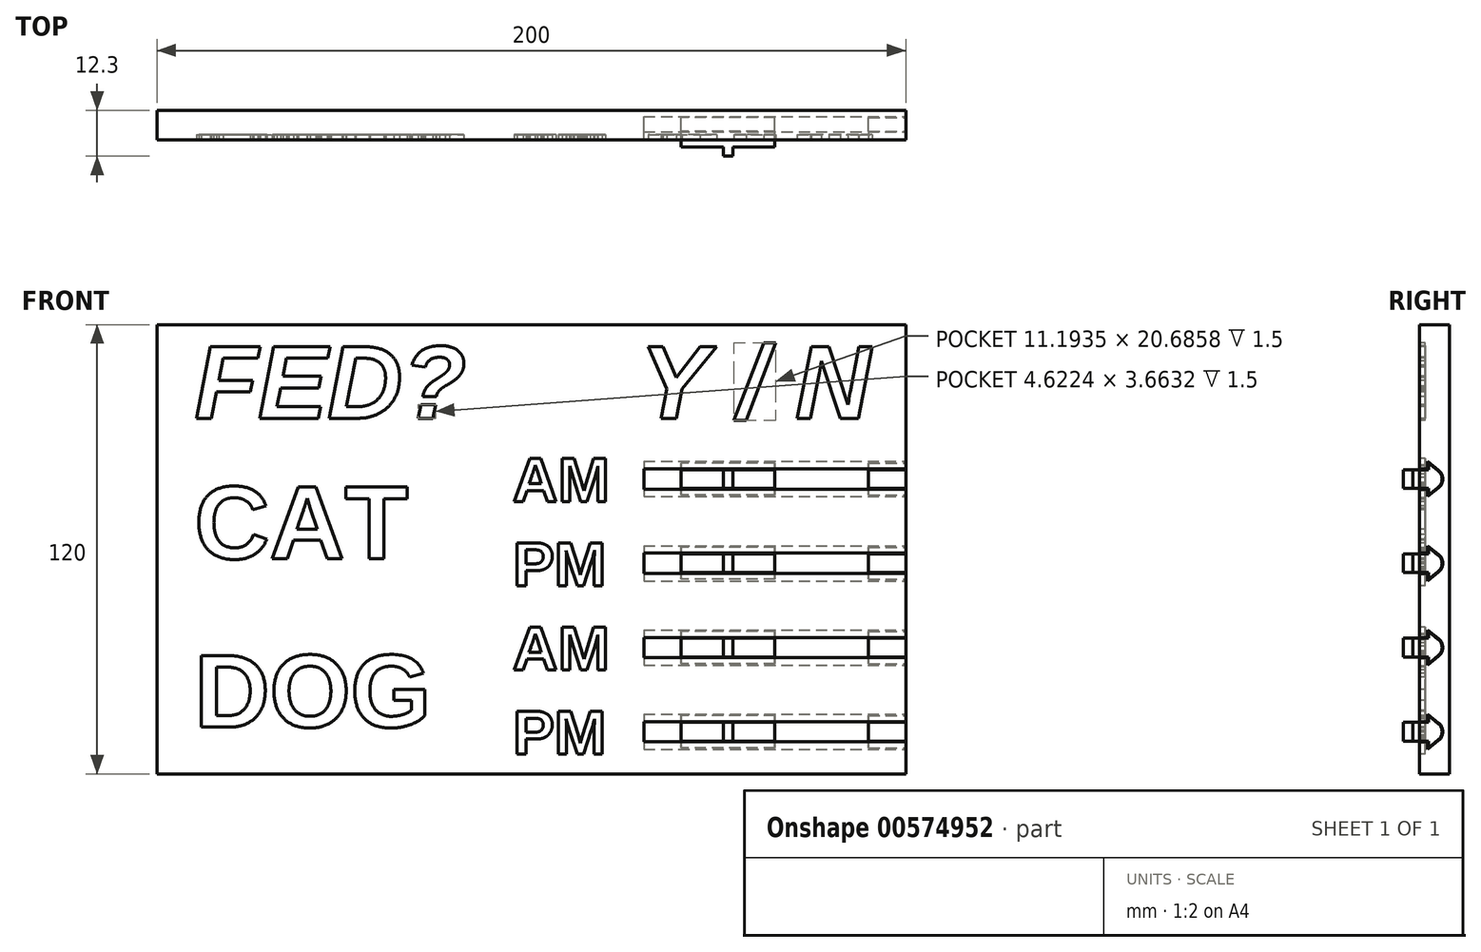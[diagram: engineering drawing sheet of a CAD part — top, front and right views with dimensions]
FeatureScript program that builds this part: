
annotation { "Feature Type Name" : "Feature", "Feature Type Description" : "" }
export const myFeature = defineFeature(function(context is Context, id is Id, definition is map)
    precondition{}
    {
        {
            var Q0;
            Q0=qCreatedBy(makeId("Front.planeOp"),FACE);
            var sketch = newSketch(context, id + "F0", { "sketchPlane" : qUnion([Q0])});
            skLineSegment(sketch, "E0.bottom", {"start": v(100, -60) * mm, "end": v(-100, -60) * mm});
            skLineSegment(sketch, "E0.top", {"start": v(100, 60) * mm, "end": v(-100, 60) * mm});
            skLineSegment(sketch, "E0.left", {"start": v(100, -60) * mm, "end": v(100, 60) * mm});
            skLineSegment(sketch, "E0.right", {"start": v(-100, -60) * mm, "end": v(-100, 60) * mm});
            skPoint(sketch, "E0.middle", {"position": v(0, 0) * mm});
            skSolve(sketch);
        }
        {
            var Q0;
            Q0=qSketchRegion(id+"F0",true);
            extrude(context, id + "F1", {"entities" : qUnion([Q0]), "depth" : 8 * mm, "offsetDistance" : 25 * mm});
        }
        {
            var Q0;
            Q0=makeQuery(id+"F1.opExtrude","CAP_FACE",FACE,{"disambiguationData":[OSD([sQuery(id+"F0.wireOp",EDGE,"E0.bottom"),sQuery(id+"F0.wireOp",EDGE,"E0.top"),sQuery(id+"F0.wireOp",EDGE,"E0.left"),sQuery(id+"F0.wireOp",EDGE,"E0.right")])],"isStart":false});
            var sketch = newSketch(context, id + "F2", { "sketchPlane" : qUnion([Q0])});
            skLineSegment(sketch, "E1", {"start": v(-100, 30) * mm, "end": v(100, 30) * mm, "construction": true});
            skLineSegment(sketch, "E2", {"start": v(-100, 7.5) * mm, "end": v(100, 7.5) * mm, "construction": true});
            skLineSegment(sketch, "E3", {"start": v(-100, -15) * mm, "end": v(100, -15) * mm, "construction": true});
            skLineSegment(sketch, "E4", {"start": v(-100, -37.5) * mm, "end": v(100, -37.5) * mm, "construction": true});
            skLineSegment(sketch, "E5", {"start": v(-100, 7.5) * mm, "end": v(-100, 30) * mm, "construction": true});
            skLineSegment(sketch, "E6", {"start": v(-100, 7.5) * mm, "end": v(-100, -15) * mm, "construction": true});
            skLineSegment(sketch, "E7", {"start": v(-100, -37.5) * mm, "end": v(-100, -15) * mm, "construction": true});
            skLineSegment(sketch, "E8", {"start": v(-100, -60) * mm, "end": v(-100, -37.5) * mm, "construction": true});
            skText(sketch, "E9", { "text": "CAT", "fontName": "Arimo-Bold.ttf"});
            skPoint(sketch, "E10", {"position": v(-90, 7.5) * mm});
            skText(sketch, "E11", { "text": "DOG", "fontName": "Arimo-Bold.ttf"});
            skPoint(sketch, "E12", {"position": v(-90, -37.5) * mm});
            skLineSegment(sketch, "E13", {"start": v(-100, 12.99) * mm, "end": v(-90, 12.99) * mm, "construction": true});
            skLineSegment(sketch, "E14", {"start": v(-100, -31.58) * mm, "end": v(-90, -31.58) * mm, "construction": true});
            skText(sketch, "E15", { "text": "FED?      Y / N", "fontName": "Arimo-BoldItalic.ttf"});
            skPoint(sketch, "E16", {"position": v(-100, 60) * mm});
            skPoint(sketch, "E17", {"position": v(-100, 45) * mm});
            skPoint(sketch, "E18", {"position": v(-90, 45) * mm});
            skLineSegment(sketch, "E19", {"start": v(-90, 50.64) * mm, "end": v(-100, 50.64) * mm, "construction": true});
            skText(sketch, "E20", { "text": "AM", "fontName": "Arimo-Bold.ttf"});
            skPoint(sketch, "E21", {"position": v(-5, 18.75) * mm});
            skText(sketch, "E22", { "text": "PM", "fontName": "Arimo-Bold.ttf"});
            skPoint(sketch, "E23", {"position": v(-5, -3.75) * mm});
            skPoint(sketch, "E24", {"position": v(20.04, -3.75) * mm});
            skPoint(sketch, "E25", {"position": v(20.96, 18.75) * mm});
            skPoint(sketch, "E26", {"position": v(100, 18.75) * mm});
            skPoint(sketch, "E27", {"position": v(100, -3.75) * mm});
            skText(sketch, "E28", { "text": "AM", "fontName": "Arimo-Bold.ttf"});
            skText(sketch, "E29", { "text": "PM", "fontName": "Arimo-Bold.ttf"});
            skPoint(sketch, "E30", {"position": v(100, -26.25) * mm});
            skPoint(sketch, "E31", {"position": v(100, -48.75) * mm});
            skPoint(sketch, "E32", {"position": v(-5, -26.25) * mm});
            skPoint(sketch, "E33", {"position": v(-5, -48.75) * mm});
            const initialGuessF2  = {"E9": [-0.09, -0.0025, 1, 0, 0.02], "E11": [-0.09, -0.0475, 1, 0, 0.02], "E15": [-0.09, 0.035, 1, 0, 0.02], "E20": [-0.005, 0.01275, 1, 0, 0.012], "E22": [-0.005, -0.00975, 1, 0, 0.012], "E28": [-0.005, -0.03225, 1, 0, 0.012], "E29": [-0.005, -0.05475, 1, 0, 0.012]};
            skSetInitialGuess(sketch, initialGuessF2);
            skSolve(sketch);
        }
        {
            var Q0;
            Q0=qSketchRegion(id+"F2",true);
            extrude(context, id + "F3", {"entities" : qUnion([Q0]), "operationType" : NewBodyOperationType.REMOVE, "oppositeDirection" : true, "depth" : 1.5 * mm, "offsetDistance" : 25 * mm});
        }
        {
            var Q0;
            Q0=makeQuery(id+"F1.opExtrude","SWEPT_FACE",FACE,{"disambiguationData":[OSD([sQuery(id+"F0.wireOp",EDGE,"E0.left")])]});
            var sketch = newSketch(context, id + "F4", { "sketchPlane" : qUnion([Q0])});
            skLineSegment(sketch, "E34", {"start": v(-8, 21.45) * mm, "end": v(-5.8, 21.45) * mm});
            skLineSegment(sketch, "E35", {"start": v(-5.8, 21.45) * mm, "end": v(-5.8, 23.45) * mm});
            skLineSegment(sketch, "E36", {"start": v(-5.8, 23.45) * mm, "end": v(-2.88, 21.08) * mm});
            skLineSegment(sketch, "E37", {"start": v(-40.2, 18.75) * mm, "end": v(26.77, 18.75) * mm, "construction": true});
            skPoint(sketch, "E38", {"position": v(-8, 18.75) * mm});
            skLineSegment(sketch, "E39", {"start": v(-8, 21.45) * mm, "end": v(-8, 18.75) * mm});
            skLineSegment(sketch, "E40.MirrorCS", {"start": v(-8, 16.05) * mm, "end": v(-8, 18.75) * mm});
            skLineSegment(sketch, "E41.MirrorCS", {"start": v(-8, 16.05) * mm, "end": v(-5.8, 16.05) * mm});
            skLineSegment(sketch, "E42.MirrorCS", {"start": v(-5.8, 16.05) * mm, "end": v(-5.8, 14.05) * mm});
            skLineSegment(sketch, "E43.MirrorCS", {"start": v(-5.8, 14.05) * mm, "end": v(-2.88, 16.42) * mm});
            skPoint(sketch, "E44.visualSharp", {"position": v(0, 18.75) * mm});
            skArc(sketch, "E44.filletArc", {"start": v(-2.88, 16.42) * mm, "mid": v(-1.77, 18.75) * mm, "end": v(-2.88, 21.08) * mm});
            skLineSegment(sketch, "E45.0", {"start": v(-7.8, 21.25) * mm, "end": v(-7.8, 21.25) * mm});
            skLineSegment(sketch, "E45.1", {"start": v(-7.8, 16.25) * mm, "end": v(-7.8, 21.25) * mm});
            skLineSegment(sketch, "E45.2", {"start": v(-7.8, 21.25) * mm, "end": v(-5.6, 21.25) * mm});
            skLineSegment(sketch, "E45.3", {"start": v(-7.8, 16.25) * mm, "end": v(-5.6, 16.25) * mm});
            skLineSegment(sketch, "E45.4", {"start": v(-5.6, 16.25) * mm, "end": v(-5.6, 14.47) * mm});
            skLineSegment(sketch, "E45.5", {"start": v(-5.6, 21.25) * mm, "end": v(-5.6, 23.03) * mm});
            skLineSegment(sketch, "E45.6", {"start": v(-5.6, 23.03) * mm, "end": v(-3, 20.93) * mm});
            skArc(sketch, "E45.7", {"start": v(-3, 16.57) * mm, "mid": v(-1.97, 18.75) * mm, "end": v(-3, 20.93) * mm});
            skLineSegment(sketch, "E45.8", {"start": v(-5.6, 14.47) * mm, "end": v(-3, 16.57) * mm});
            skPoint(sketch, "E46", {"position": v(-8, 30) * mm});
            skPoint(sketch, "E47", {"position": v(-8, 7.5) * mm});
            skPoint(sketch, "E48", {"position": v(-8, -15) * mm});
            skPoint(sketch, "E49", {"position": v(-8, -37.5) * mm});
            skLineSegment(sketch, "E50", {"start": v(-8, 30) * mm, "end": v(0, 30) * mm, "construction": true});
            skLineSegment(sketch, "E51", {"start": v(-8, 7.5) * mm, "end": v(0, 7.5) * mm, "construction": true});
            skLineSegment(sketch, "E52", {"start": v(-8, -15) * mm, "end": v(0, -15) * mm, "construction": true});
            skLineSegment(sketch, "E53", {"start": v(-8, -37.5) * mm, "end": v(0, -37.5) * mm, "construction": true});
            skPoint(sketch, "E54", {"position": v(-8, -3.75) * mm});
            skPoint(sketch, "E55", {"position": v(-8, -26.25) * mm});
            skPoint(sketch, "E56", {"position": v(-8, -48.75) * mm});
            skPoint(sketch, "E57", {"position": v(-8, -60) * mm});
            skLineSegment(sketch, "E58", {"start": v(-7.8, 21.25) * mm, "end": v(-8, 21.25) * mm});
            skLineSegment(sketch, "E59.MirrorCS", {"start": v(-7.8, 16.25) * mm, "end": v(-8, 16.25) * mm});
            skLineSegment(sketch, "E60.0.1.0", {"start": v(-5.6, 0.53) * mm, "end": v(-3, -1.57) * mm});
            skLineSegment(sketch, "E60.0.1.1", {"start": v(-5.8, -8.45) * mm, "end": v(-2.88, -6.08) * mm});
            skArc(sketch, "E60.0.1.2", {"start": v(-2.88, -6.08) * mm, "mid": v(-1.77, -3.75) * mm, "end": v(-2.88, -1.42) * mm});
            skLineSegment(sketch, "E60.0.1.3", {"start": v(-5.6, -8.03) * mm, "end": v(-3, -5.93) * mm});
            skPoint(sketch, "E60.0.1.4", {"position": v(0, -3.75) * mm});
            skArc(sketch, "E60.0.1.6", {"start": v(-3, -5.93) * mm, "mid": v(-1.97, -3.75) * mm, "end": v(-3, -1.57) * mm});
            skLineSegment(sketch, "E60.0.1.7", {"start": v(-5.8, 0.95) * mm, "end": v(-2.88, -1.42) * mm});
            skLineSegment(sketch, "E60.0.1.9", {"start": v(-7.8, -6.25) * mm, "end": v(-7.8, -1.25) * mm});
            skLineSegment(sketch, "E60.0.1.10", {"start": v(-5.6, -1.25) * mm, "end": v(-5.6, 0.53) * mm});
            skLineSegment(sketch, "E60.0.1.11", {"start": v(-5.8, -1.05) * mm, "end": v(-5.8, 0.95) * mm});
            skLineSegment(sketch, "E60.0.1.12", {"start": v(-8, -1.05) * mm, "end": v(-5.8, -1.05) * mm});
            skLineSegment(sketch, "E60.0.1.13", {"start": v(-5.6, -6.25) * mm, "end": v(-5.6, -8.03) * mm});
            skLineSegment(sketch, "E60.0.1.14", {"start": v(-7.8, -1.25) * mm, "end": v(-5.6, -1.25) * mm});
            skLineSegment(sketch, "E60.0.1.15", {"start": v(-8, -6.45) * mm, "end": v(-8, -3.75) * mm});
            skLineSegment(sketch, "E60.0.1.16", {"start": v(-5.8, -6.45) * mm, "end": v(-5.8, -8.45) * mm});
            skLineSegment(sketch, "E60.0.1.17", {"start": v(-8, -6.45) * mm, "end": v(-5.8, -6.45) * mm});
            skLineSegment(sketch, "E60.0.1.18", {"start": v(-8, -1.05) * mm, "end": v(-8, -3.75) * mm});
            skLineSegment(sketch, "E60.0.1.19", {"start": v(-7.8, -6.25) * mm, "end": v(-5.6, -6.25) * mm});
            skLineSegment(sketch, "E60.0.1.20", {"start": v(-7.8, -1.25) * mm, "end": v(-8, -1.25) * mm});
            skLineSegment(sketch, "E60.0.1.21", {"start": v(-7.8, -6.25) * mm, "end": v(-8, -6.25) * mm});
            skLineSegment(sketch, "E60.0.2.0", {"start": v(-5.6, -21.97) * mm, "end": v(-3, -24.07) * mm});
            skLineSegment(sketch, "E60.0.2.1", {"start": v(-5.8, -30.95) * mm, "end": v(-2.88, -28.58) * mm});
            skArc(sketch, "E60.0.2.2", {"start": v(-2.88, -28.58) * mm, "mid": v(-1.77, -26.25) * mm, "end": v(-2.88, -23.92) * mm});
            skLineSegment(sketch, "E60.0.2.3", {"start": v(-5.6, -30.53) * mm, "end": v(-3, -28.43) * mm});
            skPoint(sketch, "E60.0.2.4", {"position": v(0, -26.25) * mm});
            skArc(sketch, "E60.0.2.6", {"start": v(-3, -28.43) * mm, "mid": v(-1.97, -26.25) * mm, "end": v(-3, -24.07) * mm});
            skLineSegment(sketch, "E60.0.2.7", {"start": v(-5.8, -21.55) * mm, "end": v(-2.88, -23.92) * mm});
            skLineSegment(sketch, "E60.0.2.9", {"start": v(-7.8, -28.75) * mm, "end": v(-7.8, -23.75) * mm});
            skLineSegment(sketch, "E60.0.2.10", {"start": v(-5.6, -23.75) * mm, "end": v(-5.6, -21.97) * mm});
            skLineSegment(sketch, "E60.0.2.11", {"start": v(-5.8, -23.55) * mm, "end": v(-5.8, -21.55) * mm});
            skLineSegment(sketch, "E60.0.2.12", {"start": v(-8, -23.55) * mm, "end": v(-5.8, -23.55) * mm});
            skLineSegment(sketch, "E60.0.2.13", {"start": v(-5.6, -28.75) * mm, "end": v(-5.6, -30.53) * mm});
            skLineSegment(sketch, "E60.0.2.14", {"start": v(-7.8, -23.75) * mm, "end": v(-5.6, -23.75) * mm});
            skLineSegment(sketch, "E60.0.2.15", {"start": v(-8, -28.95) * mm, "end": v(-8, -26.25) * mm});
            skLineSegment(sketch, "E60.0.2.16", {"start": v(-5.8, -28.95) * mm, "end": v(-5.8, -30.95) * mm});
            skLineSegment(sketch, "E60.0.2.17", {"start": v(-8, -28.95) * mm, "end": v(-5.8, -28.95) * mm});
            skLineSegment(sketch, "E60.0.2.18", {"start": v(-8, -23.55) * mm, "end": v(-8, -26.25) * mm});
            skLineSegment(sketch, "E60.0.2.19", {"start": v(-7.8, -28.75) * mm, "end": v(-5.6, -28.75) * mm});
            skLineSegment(sketch, "E60.0.2.20", {"start": v(-7.8, -23.75) * mm, "end": v(-8, -23.75) * mm});
            skLineSegment(sketch, "E60.0.2.21", {"start": v(-7.8, -28.75) * mm, "end": v(-8, -28.75) * mm});
            skLineSegment(sketch, "E60.0.3.0", {"start": v(-5.6, -44.47) * mm, "end": v(-3, -46.57) * mm});
            skLineSegment(sketch, "E60.0.3.1", {"start": v(-5.8, -53.45) * mm, "end": v(-2.88, -51.08) * mm});
            skArc(sketch, "E60.0.3.2", {"start": v(-2.88, -51.08) * mm, "mid": v(-1.77, -48.75) * mm, "end": v(-2.88, -46.42) * mm});
            skLineSegment(sketch, "E60.0.3.3", {"start": v(-5.6, -53.03) * mm, "end": v(-3, -50.93) * mm});
            skPoint(sketch, "E60.0.3.4", {"position": v(0, -48.75) * mm});
            skArc(sketch, "E60.0.3.6", {"start": v(-3, -50.93) * mm, "mid": v(-1.97, -48.75) * mm, "end": v(-3, -46.57) * mm});
            skLineSegment(sketch, "E60.0.3.7", {"start": v(-5.8, -44.05) * mm, "end": v(-2.88, -46.42) * mm});
            skLineSegment(sketch, "E60.0.3.9", {"start": v(-7.8, -51.25) * mm, "end": v(-7.8, -46.25) * mm});
            skLineSegment(sketch, "E60.0.3.10", {"start": v(-5.6, -46.25) * mm, "end": v(-5.6, -44.47) * mm});
            skLineSegment(sketch, "E60.0.3.11", {"start": v(-5.8, -46.05) * mm, "end": v(-5.8, -44.05) * mm});
            skLineSegment(sketch, "E60.0.3.12", {"start": v(-8, -46.05) * mm, "end": v(-5.8, -46.05) * mm});
            skLineSegment(sketch, "E60.0.3.13", {"start": v(-5.6, -51.25) * mm, "end": v(-5.6, -53.03) * mm});
            skLineSegment(sketch, "E60.0.3.14", {"start": v(-7.8, -46.25) * mm, "end": v(-5.6, -46.25) * mm});
            skLineSegment(sketch, "E60.0.3.15", {"start": v(-8, -51.45) * mm, "end": v(-8, -48.75) * mm});
            skLineSegment(sketch, "E60.0.3.16", {"start": v(-5.8, -51.45) * mm, "end": v(-5.8, -53.45) * mm});
            skLineSegment(sketch, "E60.0.3.17", {"start": v(-8, -51.45) * mm, "end": v(-5.8, -51.45) * mm});
            skLineSegment(sketch, "E60.0.3.18", {"start": v(-8, -46.05) * mm, "end": v(-8, -48.75) * mm});
            skLineSegment(sketch, "E60.0.3.19", {"start": v(-7.8, -51.25) * mm, "end": v(-5.6, -51.25) * mm});
            skLineSegment(sketch, "E60.0.3.20", {"start": v(-7.8, -46.25) * mm, "end": v(-8, -46.25) * mm});
            skLineSegment(sketch, "E60.0.3.21", {"start": v(-7.8, -51.25) * mm, "end": v(-8, -51.25) * mm});
            skLineSegment(sketch, "E60.direction1", {"start": v(-8, 16.05) * mm, "end": v(0, 16.05) * mm, "construction": true});
            skLineSegment(sketch, "E60.direction2", {"start": v(-8, 16.05) * mm, "end": v(-8, -6.45) * mm, "construction": true});
            skSolve(sketch);
        }
        {
            var Q0;
            Q0=qSketchRegion(id+"F4",true);
            var Q1;
            Q1=makeQuery(id+"F4.imprint","IMPRINT",FACE,{"disambiguationData":[TD([[makeQuery(id+"F4.imprint","IMPRINT",EDGE,{"derivedFrom":sQuery(id+"F4.wireOp",EDGE,"E60.0.3.0")}),-1.0]])]});
            var Q2;
            Q2=makeQuery(id+"F4.imprint","IMPRINT",FACE,{"disambiguationData":[TD([[makeQuery(id+"F4.imprint","IMPRINT",EDGE,{"derivedFrom":sQuery(id+"F4.wireOp",EDGE,"E60.0.2.0")}),-1.0]])]});
            var Q3;
            Q3=makeQuery(id+"F4.imprint","IMPRINT",FACE,{"disambiguationData":[TD([[makeQuery(id+"F4.imprint","IMPRINT",EDGE,{"derivedFrom":sQuery(id+"F4.wireOp",EDGE,"E60.0.1.0")}),-1.0]])]});
            var Q4;
            Q4=makeQuery(id+"F4.imprint","IMPRINT",FACE,{"disambiguationData":[TD([[makeQuery(id+"F4.imprint","IMPRINT",EDGE,{"derivedFrom":sQuery(id+"F4.wireOp",EDGE,"E45.1")}),-1.0]])]});
            extrude(context, id + "F5", {"entities" : qUnion([Q0, Q1, Q2, Q3, Q4]), "operationType" : NewBodyOperationType.REMOVE, "oppositeDirection" : true, "depth" : 70 * mm, "offsetDistance" : 25 * mm});
        }
        {
            var Q0;
            {var subQ8=sQuery(id+"F4.wireOp",EDGE,"E34");Q0=makeQuery(id+"F4.imprint","IMPRINT",FACE,{"disambiguationData":[TD([[makeQuery(id+"F4.imprint","IMPRINT",EDGE,{"derivedFrom":subQ8}),1.0]])]});}
            cPlane(context, id + "F6", {"entities" : qUnion([Q0]), "cplaneType" : CPlaneType.OFFSET, "offset" : 60 * mm, "oppositeDirection" : true, "width" : 150 * mm, "height" : 150 * mm});
        }
        {
            var Q0;
            Q0=qCreatedBy(id+"F6.planeOp",FACE);
            var sketch = newSketch(context, id + "F7", { "sketchPlane" : qUnion([Q0])});
            skArc(sketch, "E61.0", {"start": v(-3, 16.57) * mm, "mid": v(-1.97, 18.75) * mm, "end": v(-3, 20.93) * mm});
            skLineSegment(sketch, "E61.1", {"start": v(-5.6, 23.03) * mm, "end": v(-3, 20.93) * mm});
            skLineSegment(sketch, "E61.2", {"start": v(-5.6, 14.47) * mm, "end": v(-3, 16.57) * mm});
            skLineSegment(sketch, "E61.3", {"start": v(-7.8, 21.25) * mm, "end": v(-5.6, 21.25) * mm});
            skLineSegment(sketch, "E61.4", {"start": v(-5.8, 14.05) * mm, "end": v(-2.88, 16.42) * mm});
            skLineSegment(sketch, "E61.5", {"start": v(-8, 16.05) * mm, "end": v(-8, 18.75) * mm});
            skLineSegment(sketch, "E61.6", {"start": v(-8, 16.05) * mm, "end": v(-5.8, 16.05) * mm});
            skLineSegment(sketch, "E61.7", {"start": v(-8, 21.45) * mm, "end": v(-5.8, 21.45) * mm});
            skLineSegment(sketch, "E61.8", {"start": v(-5.8, 23.45) * mm, "end": v(-2.88, 21.08) * mm});
            skLineSegment(sketch, "E61.9", {"start": v(-5.8, 16.05) * mm, "end": v(-5.8, 14.05) * mm});
            skLineSegment(sketch, "E61.10", {"start": v(-5.6, 21.25) * mm, "end": v(-5.6, 23.03) * mm});
            skLineSegment(sketch, "E61.11", {"start": v(-5.6, 16.25) * mm, "end": v(-5.6, 14.47) * mm});
            skLineSegment(sketch, "E61.12", {"start": v(-7.8, 16.25) * mm, "end": v(-7.8, 21.25) * mm});
            skLineSegment(sketch, "E61.13", {"start": v(-7.8, 16.25) * mm, "end": v(-5.6, 16.25) * mm});
            skLineSegment(sketch, "E61.14", {"start": v(-5.8, 21.45) * mm, "end": v(-5.8, 23.45) * mm});
            skArc(sketch, "E61.15", {"start": v(-2.88, 16.42) * mm, "mid": v(-1.77, 18.75) * mm, "end": v(-2.88, 21.08) * mm});
            skLineSegment(sketch, "E61.16", {"start": v(-8, 21.45) * mm, "end": v(-8, 18.75) * mm});
            skLineSegment(sketch, "E62.0", {"start": v(-5.6, 0.53) * mm, "end": v(-3, -1.57) * mm});
            skLineSegment(sketch, "E62.1", {"start": v(-5.8, -1.05) * mm, "end": v(-5.8, 0.95) * mm});
            skLineSegment(sketch, "E62.2", {"start": v(-5.6, -1.25) * mm, "end": v(-5.6, 0.53) * mm});
            skLineSegment(sketch, "E62.3", {"start": v(-5.6, -6.25) * mm, "end": v(-5.6, -8.03) * mm});
            skLineSegment(sketch, "E62.4", {"start": v(-8, -1.05) * mm, "end": v(-8, -3.75) * mm});
            skLineSegment(sketch, "E62.5", {"start": v(-8, -1.05) * mm, "end": v(-5.8, -1.05) * mm});
            skLineSegment(sketch, "E62.6", {"start": v(-7.8, -6.25) * mm, "end": v(-5.6, -6.25) * mm});
            skLineSegment(sketch, "E62.7", {"start": v(-5.8, -6.45) * mm, "end": v(-5.8, -8.45) * mm});
            skLineSegment(sketch, "E62.8", {"start": v(-5.6, -8.03) * mm, "end": v(-3, -5.93) * mm});
            skLineSegment(sketch, "E62.9", {"start": v(-8, -6.45) * mm, "end": v(-5.8, -6.45) * mm});
            skLineSegment(sketch, "E62.10", {"start": v(-5.8, -8.45) * mm, "end": v(-2.88, -6.08) * mm});
            skArc(sketch, "E62.11", {"start": v(-3, -5.93) * mm, "mid": v(-1.97, -3.75) * mm, "end": v(-3, -1.57) * mm});
            skLineSegment(sketch, "E62.12", {"start": v(-8, -6.45) * mm, "end": v(-8, -3.75) * mm});
            skArc(sketch, "E62.13", {"start": v(-2.88, -6.08) * mm, "mid": v(-1.77, -3.75) * mm, "end": v(-2.88, -1.42) * mm});
            skLineSegment(sketch, "E62.14", {"start": v(-7.8, -1.25) * mm, "end": v(-5.6, -1.25) * mm});
            skLineSegment(sketch, "E62.15", {"start": v(-5.8, 0.95) * mm, "end": v(-2.88, -1.42) * mm});
            skLineSegment(sketch, "E62.16", {"start": v(-7.8, -6.25) * mm, "end": v(-7.8, -1.25) * mm});
            skLineSegment(sketch, "E63.0", {"start": v(-5.8, -21.55) * mm, "end": v(-2.88, -23.92) * mm});
            skLineSegment(sketch, "E63.1", {"start": v(-7.8, -23.75) * mm, "end": v(-5.6, -23.75) * mm});
            skArc(sketch, "E63.2", {"start": v(-2.88, -28.58) * mm, "mid": v(-1.77, -26.25) * mm, "end": v(-2.88, -23.92) * mm});
            skLineSegment(sketch, "E63.3", {"start": v(-8, -28.95) * mm, "end": v(-8, -26.25) * mm});
            skLineSegment(sketch, "E63.4", {"start": v(-5.6, -23.75) * mm, "end": v(-5.6, -21.97) * mm});
            skLineSegment(sketch, "E63.5", {"start": v(-5.8, -28.95) * mm, "end": v(-5.8, -30.95) * mm});
            skLineSegment(sketch, "E63.6", {"start": v(-5.6, -21.97) * mm, "end": v(-3, -24.07) * mm});
            skArc(sketch, "E63.7", {"start": v(-3, -28.43) * mm, "mid": v(-1.97, -26.25) * mm, "end": v(-3, -24.07) * mm});
            skLineSegment(sketch, "E63.8", {"start": v(-8, -23.55) * mm, "end": v(-5.8, -23.55) * mm});
            skLineSegment(sketch, "E63.9", {"start": v(-5.8, -30.95) * mm, "end": v(-2.88, -28.58) * mm});
            skLineSegment(sketch, "E63.10", {"start": v(-5.6, -28.75) * mm, "end": v(-5.6, -30.53) * mm});
            skLineSegment(sketch, "E63.11", {"start": v(-7.8, -28.75) * mm, "end": v(-5.6, -28.75) * mm});
            skLineSegment(sketch, "E63.12", {"start": v(-5.8, -23.55) * mm, "end": v(-5.8, -21.55) * mm});
            skLineSegment(sketch, "E63.13", {"start": v(-8, -28.95) * mm, "end": v(-5.8, -28.95) * mm});
            skLineSegment(sketch, "E63.14", {"start": v(-8, -23.55) * mm, "end": v(-8, -26.25) * mm});
            skLineSegment(sketch, "E63.15", {"start": v(-5.6, -30.53) * mm, "end": v(-3, -28.43) * mm});
            skLineSegment(sketch, "E63.16", {"start": v(-7.8, -28.75) * mm, "end": v(-7.8, -23.75) * mm});
            skLineSegment(sketch, "E64.0", {"start": v(-7.8, -51.25) * mm, "end": v(-7.8, -46.25) * mm});
            skLineSegment(sketch, "E64.1", {"start": v(-5.8, -53.45) * mm, "end": v(-2.88, -51.08) * mm});
            skLineSegment(sketch, "E64.2", {"start": v(-8, -46.05) * mm, "end": v(-5.8, -46.05) * mm});
            skLineSegment(sketch, "E64.3", {"start": v(-5.6, -46.25) * mm, "end": v(-5.6, -44.47) * mm});
            skArc(sketch, "E64.4", {"start": v(-2.88, -51.08) * mm, "mid": v(-1.77, -48.75) * mm, "end": v(-2.88, -46.42) * mm});
            skLineSegment(sketch, "E64.5", {"start": v(-5.6, -51.25) * mm, "end": v(-5.6, -53.03) * mm});
            skLineSegment(sketch, "E64.6", {"start": v(-5.8, -46.05) * mm, "end": v(-5.8, -44.05) * mm});
            skLineSegment(sketch, "E64.7", {"start": v(-5.8, -51.45) * mm, "end": v(-5.8, -53.45) * mm});
            skLineSegment(sketch, "E64.8", {"start": v(-5.6, -53.03) * mm, "end": v(-3, -50.93) * mm});
            skLineSegment(sketch, "E64.9", {"start": v(-7.8, -46.25) * mm, "end": v(-5.6, -46.25) * mm});
            skLineSegment(sketch, "E64.10", {"start": v(-8, -51.45) * mm, "end": v(-5.8, -51.45) * mm});
            skLineSegment(sketch, "E64.11", {"start": v(-8, -51.45) * mm, "end": v(-8, -48.75) * mm});
            skLineSegment(sketch, "E64.12", {"start": v(-8, -46.05) * mm, "end": v(-8, -48.75) * mm});
            skLineSegment(sketch, "E64.13", {"start": v(-5.8, -44.05) * mm, "end": v(-2.88, -46.42) * mm});
            skArc(sketch, "E64.14", {"start": v(-3, -50.93) * mm, "mid": v(-1.97, -48.75) * mm, "end": v(-3, -46.57) * mm});
            skLineSegment(sketch, "E64.15", {"start": v(-7.8, -51.25) * mm, "end": v(-5.6, -51.25) * mm});
            skLineSegment(sketch, "E64.16", {"start": v(-5.6, -44.47) * mm, "end": v(-3, -46.57) * mm});
            skSolve(sketch);
        }
        {
            var Q0;
            Q0=makeQuery(id+"F7.imprint","IMPRINT",FACE,{"disambiguationData":[TD([[makeQuery(id+"F7.imprint","IMPRINT",EDGE,{"derivedFrom":sQuery(id+"F7.wireOp",EDGE,"E61.0")}),1.0]])]});
            var Q1;
            Q1=makeQuery(id+"F7.imprint","IMPRINT",FACE,{"disambiguationData":[TD([[makeQuery(id+"F7.imprint","IMPRINT",EDGE,{"derivedFrom":sQuery(id+"F7.wireOp",EDGE,"E62.0")}),-1.0]])]});
            var Q2;
            Q2=makeQuery(id+"F7.imprint","IMPRINT",FACE,{"disambiguationData":[TD([[makeQuery(id+"F7.imprint","IMPRINT",EDGE,{"derivedFrom":sQuery(id+"F7.wireOp",EDGE,"E63.1")}),-1.0]])]});
            var Q3;
            Q3=makeQuery(id+"F7.imprint","IMPRINT",FACE,{"disambiguationData":[TD([[makeQuery(id+"F7.imprint","IMPRINT",EDGE,{"derivedFrom":sQuery(id+"F7.wireOp",EDGE,"E64.0")}),-1.0]])]});
            extrude(context, id + "F8", {"entities" : qUnion([Q0, Q1, Q2, Q3]), "depth" : 25 * mm, "offsetDistance" : 25 * mm});
        }
        {
            var Q0;
            Q0=makeQuery(id+"F8.opExtrude","SWEPT_FACE",FACE,{"disambiguationData":[OSD([sQuery(id+"F7.wireOp",EDGE,"E61.12")])]});
            var Q1;
            Q1=makeQuery(id+"F8.opExtrude","SWEPT_FACE",FACE,{"disambiguationData":[OSD([sQuery(id+"F7.wireOp",EDGE,"E62.16")])]});
            var Q2;
            Q2=makeQuery(id+"F8.opExtrude","SWEPT_FACE",FACE,{"disambiguationData":[OSD([sQuery(id+"F7.wireOp",EDGE,"E64.0")])]});
            var Q3;
            Q3=makeQuery(id+"F8.opExtrude","SWEPT_FACE",FACE,{"disambiguationData":[OSD([sQuery(id+"F7.wireOp",EDGE,"E63.16")])]});
            extrude(context, id + "F9", {"entities" : qUnion([Q0, Q1, Q2, Q3]), "operationType" : NewBodyOperationType.ADD, "depth" : 2 * mm, "offsetDistance" : 25 * mm});
        }
        {
            var Q0;
            Q0=makeQuery(id+"F4.imprint","IMPRINT",FACE,{"disambiguationData":[TD([[makeQuery(id+"F4.imprint","IMPRINT",EDGE,{"derivedFrom":sQuery(id+"F4.wireOp",EDGE,"E45.1")}),-1.0]])]});
            var Q1;
            Q1=makeQuery(id+"F4.imprint","IMPRINT",FACE,{"disambiguationData":[TD([[makeQuery(id+"F4.imprint","IMPRINT",EDGE,{"derivedFrom":sQuery(id+"F4.wireOp",EDGE,"E45.1")}),1.0]])]});
            var Q2;
            Q2=makeQuery(id+"F4.imprint","IMPRINT",FACE,{"disambiguationData":[TD([[makeQuery(id+"F4.imprint","IMPRINT",EDGE,{"derivedFrom":sQuery(id+"F4.wireOp",EDGE,"E60.0.1.9")}),1.0]])]});
            var Q3;
            Q3=makeQuery(id+"F4.imprint","IMPRINT",FACE,{"disambiguationData":[TD([[makeQuery(id+"F4.imprint","IMPRINT",EDGE,{"derivedFrom":sQuery(id+"F4.wireOp",EDGE,"E60.0.1.0")}),-1.0]])]});
            var Q4;
            Q4=makeQuery(id+"F4.imprint","IMPRINT",FACE,{"disambiguationData":[TD([[makeQuery(id+"F4.imprint","IMPRINT",EDGE,{"derivedFrom":sQuery(id+"F4.wireOp",EDGE,"E60.0.2.9")}),1.0]])]});
            var Q5;
            Q5=makeQuery(id+"F4.imprint","IMPRINT",FACE,{"disambiguationData":[TD([[makeQuery(id+"F4.imprint","IMPRINT",EDGE,{"derivedFrom":sQuery(id+"F4.wireOp",EDGE,"E60.0.2.0")}),-1.0]])]});
            var Q6;
            Q6=makeQuery(id+"F4.imprint","IMPRINT",FACE,{"disambiguationData":[TD([[makeQuery(id+"F4.imprint","IMPRINT",EDGE,{"derivedFrom":sQuery(id+"F4.wireOp",EDGE,"E60.0.3.9")}),1.0]])]});
            var Q7;
            Q7=makeQuery(id+"F4.imprint","IMPRINT",FACE,{"disambiguationData":[TD([[makeQuery(id+"F4.imprint","IMPRINT",EDGE,{"derivedFrom":sQuery(id+"F4.wireOp",EDGE,"E60.0.3.0")}),-1.0]])]});
            extrude(context, id + "F10", {"entities" : qUnion([Q0, Q1, Q2, Q3, Q4, Q5, Q6, Q7]), "oppositeDirection" : true, "depth" : 10 * mm, "offsetDistance" : 25 * mm});
        }
        {
            var Q0;
            {var subQ0=sQuery(id+"F7.wireOp",EDGE,"E61.3");Q0=makeQuery(id+"F9.boolean.opBoolean","MERGE",FACE,{"derivedFrom":[makeQuery(id+"F8.opExtrude","SWEPT_FACE",FACE,{"disambiguationData":[OSD([subQ0])]}),makeQuery(id+"F9.opExtrude","SWEPT_FACE",FACE,{"disambiguationData":[OSD([subQ0,sQuery(id+"F7.wireOp",EDGE,"E61.12")])]})]});}
            cPlane(context, id + "F11", {"entities" : qUnion([Q0]), "cplaneType" : CPlaneType.OFFSET, "offset" : 0 * mm, "width" : 150 * mm, "height" : 150 * mm});
        }
        {
            var Q0;
            {var subQ0=sQuery(id+"F7.wireOp",EDGE,"E62.14");Q0=makeQuery(id+"F9.boolean.opBoolean","MERGE",FACE,{"derivedFrom":[makeQuery(id+"F8.opExtrude","SWEPT_FACE",FACE,{"disambiguationData":[OSD([subQ0])]}),makeQuery(id+"F9.opExtrude","SWEPT_FACE",FACE,{"disambiguationData":[OSD([subQ0,sQuery(id+"F7.wireOp",EDGE,"E62.16")])]})]});}
            cPlane(context, id + "F12", {"entities" : qUnion([Q0]), "cplaneType" : CPlaneType.OFFSET, "offset" : 0 * mm, "width" : 150 * mm, "height" : 150 * mm});
        }
        {
            var Q0;
            {var subQ0=sQuery(id+"F7.wireOp",EDGE,"E63.1");Q0=makeQuery(id+"F9.boolean.opBoolean","MERGE",FACE,{"derivedFrom":[makeQuery(id+"F8.opExtrude","SWEPT_FACE",FACE,{"disambiguationData":[OSD([subQ0])]}),makeQuery(id+"F9.opExtrude","SWEPT_FACE",FACE,{"disambiguationData":[OSD([subQ0,sQuery(id+"F7.wireOp",EDGE,"E63.16")])]})]});}
            cPlane(context, id + "F13", {"entities" : qUnion([Q0]), "cplaneType" : CPlaneType.OFFSET, "offset" : 0 * mm, "width" : 150 * mm, "height" : 150 * mm});
        }
        {
            var Q0;
            {var subQ0=sQuery(id+"F7.wireOp",EDGE,"E64.9");Q0=makeQuery(id+"F9.boolean.opBoolean","MERGE",FACE,{"derivedFrom":[makeQuery(id+"F8.opExtrude","SWEPT_FACE",FACE,{"disambiguationData":[OSD([subQ0])]}),makeQuery(id+"F9.opExtrude","SWEPT_FACE",FACE,{"disambiguationData":[OSD([sQuery(id+"F7.wireOp",EDGE,"E64.0"),subQ0])]})]});}
            cPlane(context, id + "F14", {"entities" : qUnion([Q0]), "cplaneType" : CPlaneType.OFFSET, "offset" : 0 * mm, "width" : 150 * mm, "height" : 150 * mm});
        }
        {
            var Q0;
            Q0=qCreatedBy(id+"F11.planeOp",FACE);
            var sketch = newSketch(context, id + "F15", { "sketchPlane" : qUnion([Q0])});
            skLineSegment(sketch, "E65.bottom", {"start": v(53.75, -9.8) * mm, "end": v(51.25, -9.8) * mm});
            skLineSegment(sketch, "E65.top", {"start": v(53.75, -12.3) * mm, "end": v(51.25, -12.3) * mm});
            skLineSegment(sketch, "E65.left", {"start": v(53.75, -9.8) * mm, "end": v(53.75, -12.3) * mm});
            skLineSegment(sketch, "E65.right", {"start": v(51.25, -9.8) * mm, "end": v(51.25, -12.3) * mm});
            skPoint(sketch, "E65.middle", {"position": v(52.5, -11.05) * mm});
            skSolve(sketch);
        }
        {
            var Q0;
            Q0=makeQuery(id+"F15.imprint","IMPRINT",FACE,{"disambiguationData":[TD([[makeQuery(id+"F15.imprint","IMPRINT",EDGE,{"derivedFrom":sQuery(id+"F15.wireOp",EDGE,"E65.bottom")}),1.0]])]});
            var Q1;
            {var subQ0=sQuery(id+"F7.wireOp",EDGE,"E61.13");Q1=makeQuery(id+"F9.boolean.opBoolean","MERGE",FACE,{"derivedFrom":[makeQuery(id+"F8.opExtrude","SWEPT_FACE",FACE,{"disambiguationData":[OSD([subQ0])]}),makeQuery(id+"F9.opExtrude","SWEPT_FACE",FACE,{"disambiguationData":[OSD([sQuery(id+"F7.wireOp",EDGE,"E61.12"),subQ0])]})]});}
            extrude(context, id + "F16", {"entities" : qUnion([Q0]), "operationType" : NewBodyOperationType.ADD, "endBound" : BoundingType.UP_TO_SURFACE, "oppositeDirection" : true, "depth" : 25 * mm, "endBoundEntityFace" : qUnion([Q1]), "offsetDistance" : 25 * mm});
        }
        {
            var Q0;
            Q0=qCreatedBy(id+"F12.planeOp",FACE);
            var sketch = newSketch(context, id + "F17", { "sketchPlane" : qUnion([Q0])});
            skLineSegment(sketch, "E66.0", {"start": v(51.25, -9.8) * mm, "end": v(51.25, -12.3) * mm});
            skLineSegment(sketch, "E66.1", {"start": v(53.75, -9.8) * mm, "end": v(53.75, -12.3) * mm});
            skLineSegment(sketch, "E66.2", {"start": v(53.75, -12.3) * mm, "end": v(51.25, -12.3) * mm});
            skLineSegment(sketch, "E66.3", {"start": v(53.75, -9.8) * mm, "end": v(51.25, -9.8) * mm});
            skSolve(sketch);
        }
        {
            var Q0;
            Q0=qSketchRegion(id+"F17",true);
            var Q1;
            {var subQ0=sQuery(id+"F7.wireOp",EDGE,"E62.6");Q1=makeQuery(id+"F9.boolean.opBoolean","MERGE",FACE,{"derivedFrom":[makeQuery(id+"F8.opExtrude","SWEPT_FACE",FACE,{"disambiguationData":[OSD([subQ0])]}),makeQuery(id+"F9.opExtrude","SWEPT_FACE",FACE,{"disambiguationData":[OSD([subQ0,sQuery(id+"F7.wireOp",EDGE,"E62.16")])]})]});}
            extrude(context, id + "F18", {"entities" : qUnion([Q0]), "operationType" : NewBodyOperationType.ADD, "endBound" : BoundingType.UP_TO_SURFACE, "oppositeDirection" : true, "depth" : 25 * mm, "endBoundEntityFace" : qUnion([Q1]), "offsetDistance" : 25 * mm});
        }
        {
            var Q0;
            Q0=qCreatedBy(id+"F13.planeOp",FACE);
            var sketch = newSketch(context, id + "F19", { "sketchPlane" : qUnion([Q0])});
            skLineSegment(sketch, "E67.0", {"start": v(51.25, -9.8) * mm, "end": v(51.25, -12.3) * mm});
            skLineSegment(sketch, "E67.1", {"start": v(53.75, -9.8) * mm, "end": v(53.75, -12.3) * mm});
            skLineSegment(sketch, "E67.2", {"start": v(53.75, -12.3) * mm, "end": v(51.25, -12.3) * mm});
            skLineSegment(sketch, "E67.3", {"start": v(53.75, -9.8) * mm, "end": v(51.25, -9.8) * mm});
            skSolve(sketch);
        }
        {
            var Q0;
            Q0=makeQuery(id+"F19.imprint","IMPRINT",FACE,{"disambiguationData":[TD([[makeQuery(id+"F19.imprint","IMPRINT",EDGE,{"derivedFrom":sQuery(id+"F19.wireOp",EDGE,"E67.0")}),1.0]])]});
            var Q1;
            {var subQ0=sQuery(id+"F7.wireOp",EDGE,"E63.11");Q1=makeQuery(id+"F9.boolean.opBoolean","MERGE",FACE,{"derivedFrom":[makeQuery(id+"F8.opExtrude","SWEPT_FACE",FACE,{"disambiguationData":[OSD([subQ0])]}),makeQuery(id+"F9.opExtrude","SWEPT_FACE",FACE,{"disambiguationData":[OSD([subQ0,sQuery(id+"F7.wireOp",EDGE,"E63.16")])]})]});}
            extrude(context, id + "F20", {"entities" : qUnion([Q0]), "operationType" : NewBodyOperationType.ADD, "endBound" : BoundingType.UP_TO_SURFACE, "oppositeDirection" : true, "depth" : 25 * mm, "endBoundEntityFace" : qUnion([Q1]), "offsetDistance" : 25 * mm});
        }
        {
            var Q0;
            Q0=qCreatedBy(id+"F14.planeOp",FACE);
            var sketch = newSketch(context, id + "F21", { "sketchPlane" : qUnion([Q0])});
            skLineSegment(sketch, "E68.0", {"start": v(51.25, -9.8) * mm, "end": v(51.25, -12.3) * mm});
            skLineSegment(sketch, "E68.1", {"start": v(53.75, -9.8) * mm, "end": v(53.75, -12.3) * mm});
            skLineSegment(sketch, "E68.2", {"start": v(53.75, -12.3) * mm, "end": v(51.25, -12.3) * mm});
            skLineSegment(sketch, "E68.3", {"start": v(53.75, -9.8) * mm, "end": v(51.25, -9.8) * mm});
            skSolve(sketch);
        }
        {
            var Q0;
            Q0=qSketchRegion(id+"F21",true);
            var Q1;
            {var subQ0=sQuery(id+"F7.wireOp",EDGE,"E64.15");Q1=makeQuery(id+"F9.boolean.opBoolean","MERGE",FACE,{"derivedFrom":[makeQuery(id+"F8.opExtrude","SWEPT_FACE",FACE,{"disambiguationData":[OSD([subQ0])]}),makeQuery(id+"F9.opExtrude","SWEPT_FACE",FACE,{"disambiguationData":[OSD([sQuery(id+"F7.wireOp",EDGE,"E64.0"),subQ0])]})]});}
            extrude(context, id + "F22", {"entities" : qUnion([Q0]), "operationType" : NewBodyOperationType.ADD, "endBound" : BoundingType.UP_TO_SURFACE, "oppositeDirection" : true, "depth" : 25 * mm, "endBoundEntityFace" : qUnion([Q1]), "offsetDistance" : 25 * mm});
        }
    });
